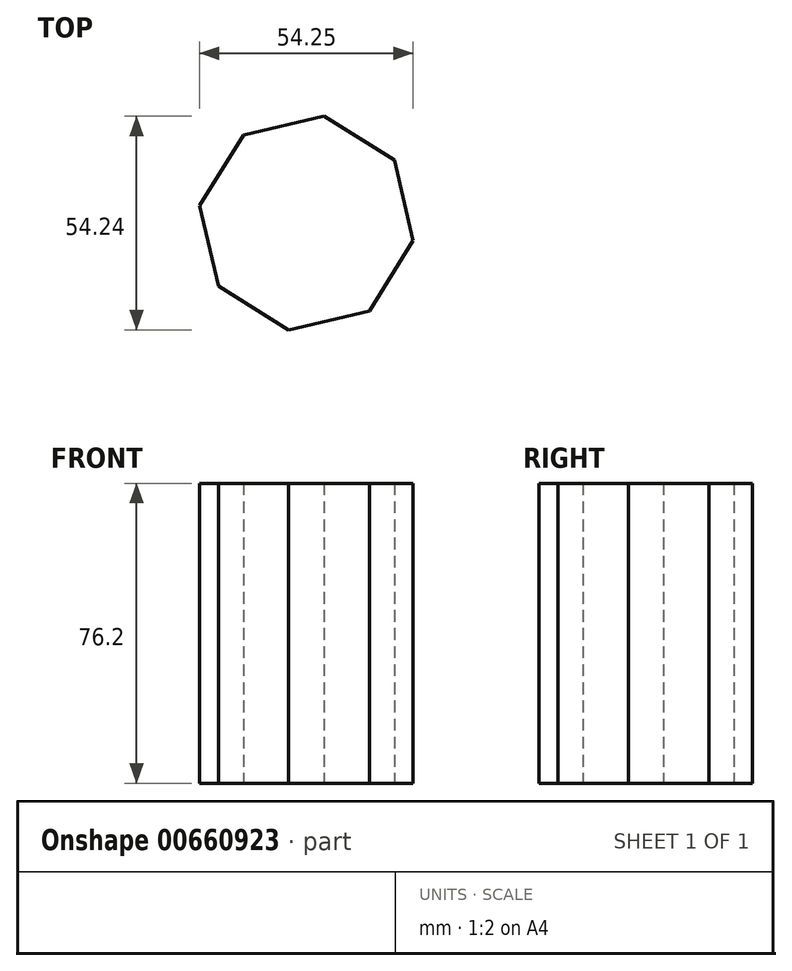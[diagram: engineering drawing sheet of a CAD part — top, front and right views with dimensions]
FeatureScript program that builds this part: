
annotation { "Feature Type Name" : "Feature", "Feature Type Description" : "" }
export const myFeature = defineFeature(function(context is Context, id is Id, definition is map)
    precondition{}
    {
        {
            var Q0;
            Q0=qCreatedBy(makeId("Top.planeOp"),FACE);
            var sketch = newSketch(context, id + "F0", { "sketchPlane" : qUnion([Q0])});
            skCircle(sketch, "E0.cCircle", {"center": v(-41.37, 40.2) * mm, "radius": 25.4 * mm, "construction": true});
            skLineSegment(sketch, "E0.0", {"start": v(-14.24, 35.71) * mm, "end": v(-25.36, 17.85) * mm});
            skLineSegment(sketch, "E0.1", {"start": v(-25.36, 17.85) * mm, "end": v(-45.85, 13.08) * mm});
            skLineSegment(sketch, "E0.2", {"start": v(-45.85, 13.08) * mm, "end": v(-63.72, 24.2) * mm});
            skLineSegment(sketch, "E0.3", {"start": v(-63.72, 24.2) * mm, "end": v(-68.5, 44.69) * mm});
            skLineSegment(sketch, "E0.4", {"start": v(-68.5, 44.69) * mm, "end": v(-57.37, 62.55) * mm});
            skLineSegment(sketch, "E0.5", {"start": v(-57.37, 62.55) * mm, "end": v(-36.88, 67.32) * mm});
            skLineSegment(sketch, "E0.6", {"start": v(-36.88, 67.32) * mm, "end": v(-19.01, 56.2) * mm});
            skLineSegment(sketch, "E0.7", {"start": v(-19.01, 56.2) * mm, "end": v(-14.24, 35.71) * mm});
            skPoint(sketch, "E0.0.midPoint", {"position": v(-19.8, 26.78) * mm});
            skSolve(sketch);
        }
        {
            var Q0;
            Q0 = qSketchRegion(id + "F0", true);
            extrude(context, id + "F1", {"entities" : qUnion([Q0]), "depth" : 76.2 * mm, "offsetDistance" : 25.4 * mm});
        }
    });
